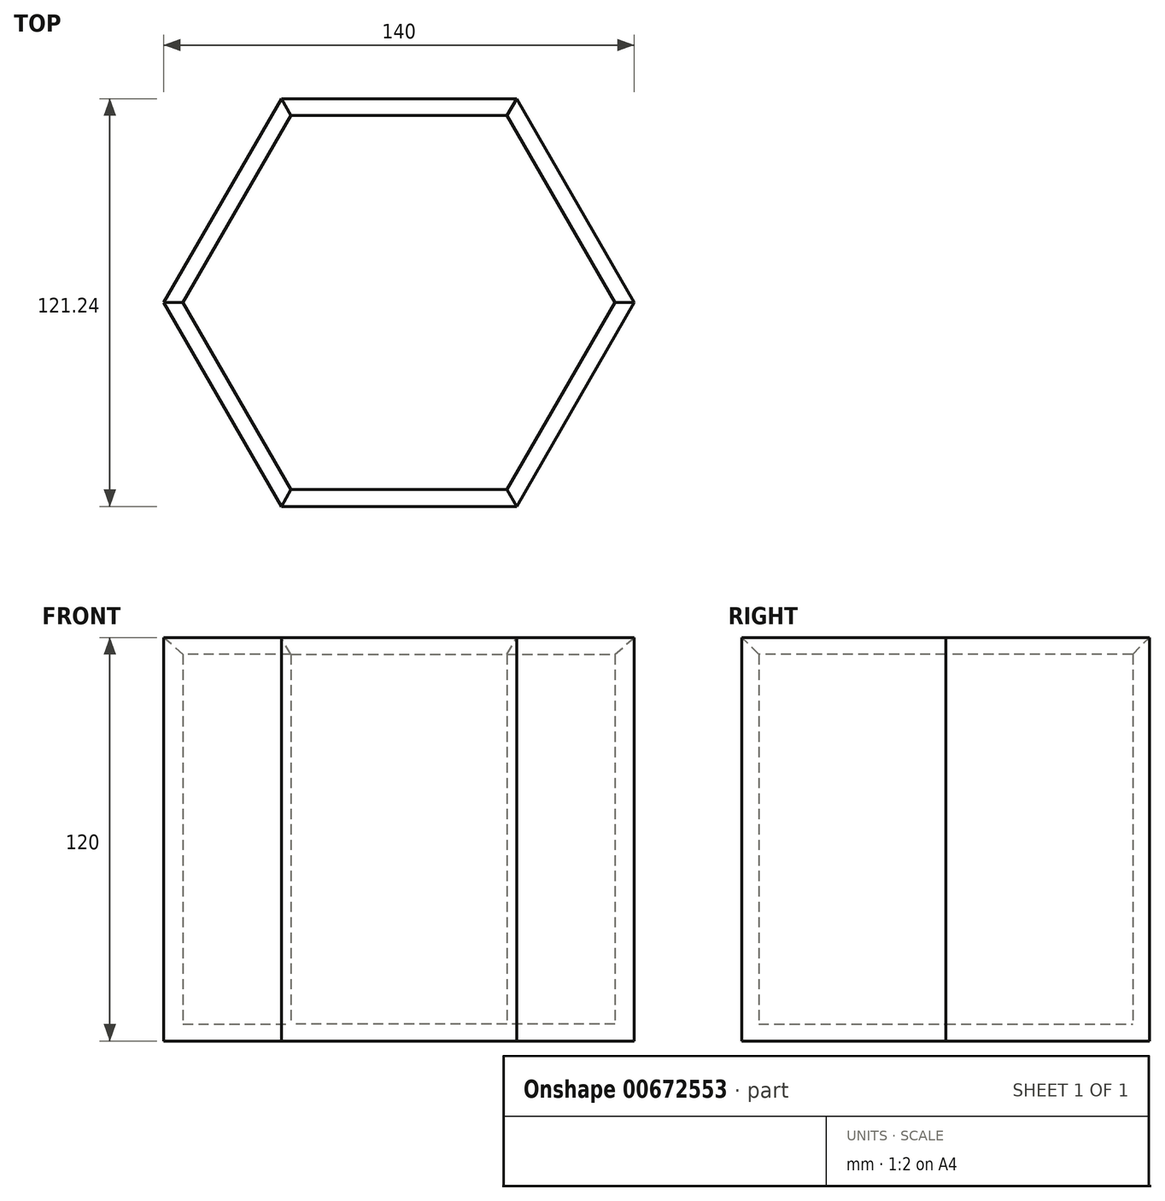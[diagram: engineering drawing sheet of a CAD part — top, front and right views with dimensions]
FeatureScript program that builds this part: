
annotation { "Feature Type Name" : "Feature", "Feature Type Description" : "" }
export const myFeature = defineFeature(function(context is Context, id is Id, definition is map)
    precondition{}
    {
        {
            var Q0;
            Q0=qCreatedBy(makeId("Top.planeOp"),FACE);
            var sketch = newSketch(context, id + "F0", { "sketchPlane" : qUnion([Q0])});
            skCircle(sketch, "E0.cCircle", {"center": v(0, 0) * mm, "radius": 70 * mm, "construction": true});
            skLineSegment(sketch, "E0.0", {"start": v(70, 0) * mm, "end": v(35, -60.62) * mm});
            skLineSegment(sketch, "E0.1", {"start": v(35, -60.62) * mm, "end": v(-35, -60.62) * mm});
            skLineSegment(sketch, "E0.2", {"start": v(-35, -60.62) * mm, "end": v(-70, 0) * mm});
            skLineSegment(sketch, "E0.3", {"start": v(-70, 0) * mm, "end": v(-35, 60.62) * mm});
            skLineSegment(sketch, "E0.4", {"start": v(-35, 60.62) * mm, "end": v(35, 60.62) * mm});
            skLineSegment(sketch, "E0.5", {"start": v(35, 60.62) * mm, "end": v(70, 0) * mm});
            skLineSegment(sketch, "E1.0", {"start": v(-32.11, -55.62) * mm, "end": v(-64.23, 0) * mm});
            skLineSegment(sketch, "E1.1", {"start": v(-32.11, 55.62) * mm, "end": v(32.11, 55.62) * mm});
            skLineSegment(sketch, "E1.2", {"start": v(32.11, 55.62) * mm, "end": v(64.23, 0) * mm});
            skLineSegment(sketch, "E1.3", {"start": v(-64.23, 0) * mm, "end": v(-32.11, 55.62) * mm});
            skLineSegment(sketch, "E1.4", {"start": v(64.23, 0) * mm, "end": v(32.11, -55.62) * mm});
            skLineSegment(sketch, "E1.5", {"start": v(32.11, -55.62) * mm, "end": v(-32.11, -55.62) * mm});
            skSolve(sketch);
        }
        {
            var Q0;
            Q0=makeQuery(id+"F0.imprint","IMPRINT",FACE,{"disambiguationData":[TD([[makeQuery(id+"F0.imprint","IMPRINT",EDGE,{"derivedFrom":sQuery(id+"F0.wireOp",EDGE,"E1.0")}),-1.0]])]});
            extrude(context, id + "F1", {"entities" : qUnion([Q0]), "depth" : 5 * mm, "offsetDistance" : 25 * mm});
        }
        {
            var Q0;
            Q0 = qSketchRegion(id + "F0", true);
            extrude(context, id + "F2", {"entities" : qUnion([Q0]), "operationType" : NewBodyOperationType.ADD, "depth" : 120 * mm, "offsetDistance" : 25 * mm});
        }
        {
            var Q0;
            Q0=makeQuery(id+"F2.opExtrude","CAP_EDGE",EDGE,{"disambiguationData":[OSD([sQuery(id+"F0.wireOp",EDGE,"E1.5")])],"isStart":false});
            var Q1;
            Q1=makeQuery(id+"F2.opExtrude","CAP_EDGE",EDGE,{"disambiguationData":[OSD([sQuery(id+"F0.wireOp",EDGE,"E1.0")])],"isStart":false});
            var Q2;
            Q2=makeQuery(id+"F2.opExtrude","CAP_EDGE",EDGE,{"disambiguationData":[OSD([sQuery(id+"F0.wireOp",EDGE,"E1.3")])],"isStart":false});
            var Q3;
            Q3=makeQuery(id+"F2.opExtrude","CAP_EDGE",EDGE,{"disambiguationData":[OSD([sQuery(id+"F0.wireOp",EDGE,"E1.1")])],"isStart":false});
            var Q4;
            Q4=makeQuery(id+"F2.opExtrude","CAP_EDGE",EDGE,{"disambiguationData":[OSD([sQuery(id+"F0.wireOp",EDGE,"E1.2")])],"isStart":false});
            var Q5;
            Q5=makeQuery(id+"F2.opExtrude","CAP_EDGE",EDGE,{"disambiguationData":[OSD([sQuery(id+"F0.wireOp",EDGE,"E1.4")])],"isStart":false});
            chamfer(context, id + "F3", {"entities" : qUnion([Q0, Q1, Q2, Q3, Q4, Q5]), "width" : 5 * mm, "tangentPropagation" : true});
        }
    });
